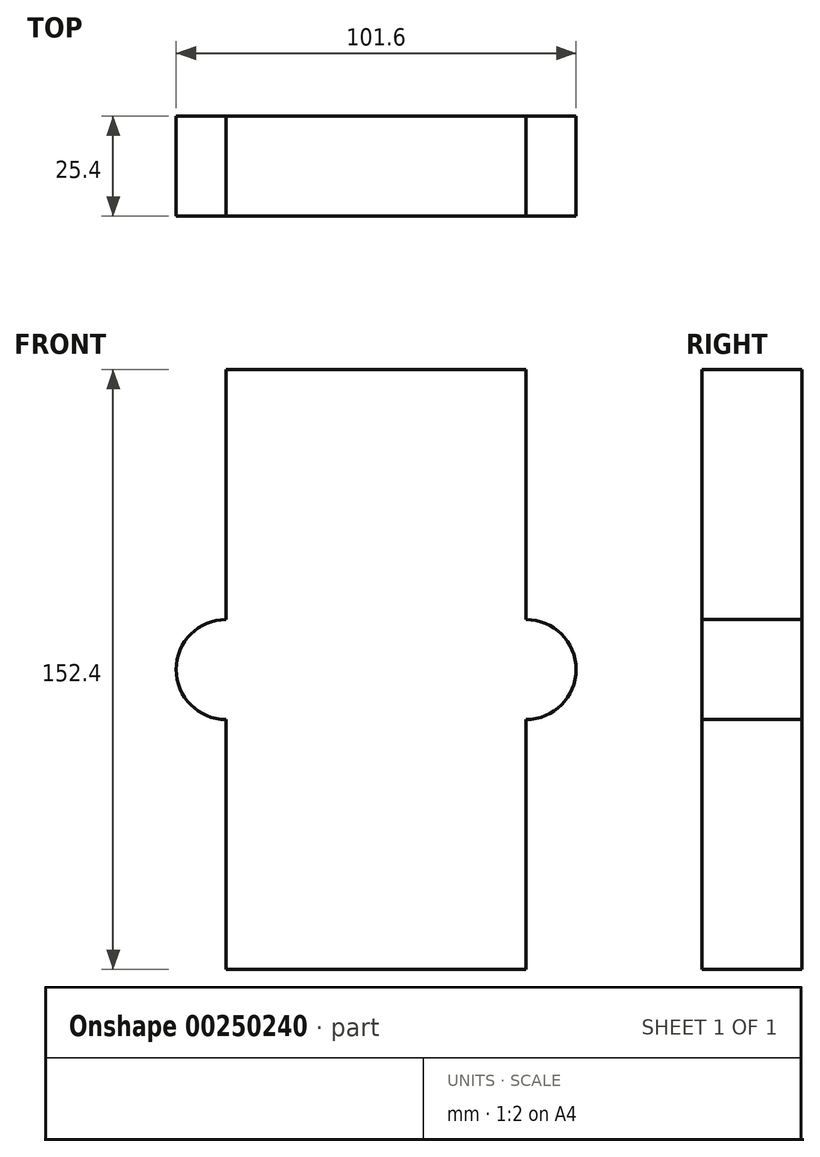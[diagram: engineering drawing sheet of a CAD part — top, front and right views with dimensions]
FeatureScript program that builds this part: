
annotation { "Feature Type Name" : "Feature", "Feature Type Description" : "" }
export const myFeature = defineFeature(function(context is Context, id is Id, definition is map)
    precondition{}
    {
        {
            var Q0;
            Q0=qCreatedBy(makeId("Front.planeOp"),FACE);
            var sketch = newSketch(context, id + "F0", { "sketchPlane" : qUnion([Q0])});
            skLineSegment(sketch, "E0.bottom", {"start": v(38.1, -76.2) * mm, "end": v(-38.1, -76.2) * mm});
            skLineSegment(sketch, "E0.top", {"start": v(38.1, 76.2) * mm, "end": v(-38.1, 76.2) * mm});
            skLineSegment(sketch, "E0.left", {"start": v(38.1, -76.2) * mm, "end": v(38.1, 76.2) * mm});
            skLineSegment(sketch, "E0.right", {"start": v(-38.1, -76.2) * mm, "end": v(-38.1, 76.2) * mm});
            skPoint(sketch, "E0.middle", {"position": v(0, 0) * mm});
            skCircle(sketch, "E1", {"center": v(-38.1, 0) * mm, "radius": 12.7 * mm});
            skCircle(sketch, "E2", {"center": v(38.1, 0) * mm, "radius": 12.7 * mm});
            skSolve(sketch);
        }
        {
            var Q0;
            Q0 = qSketchRegion(id + "F0", true);
            extrude(context, id + "F1", {"entities" : qUnion([Q0]), "depth" : 25.4 * mm});
        }
    });
